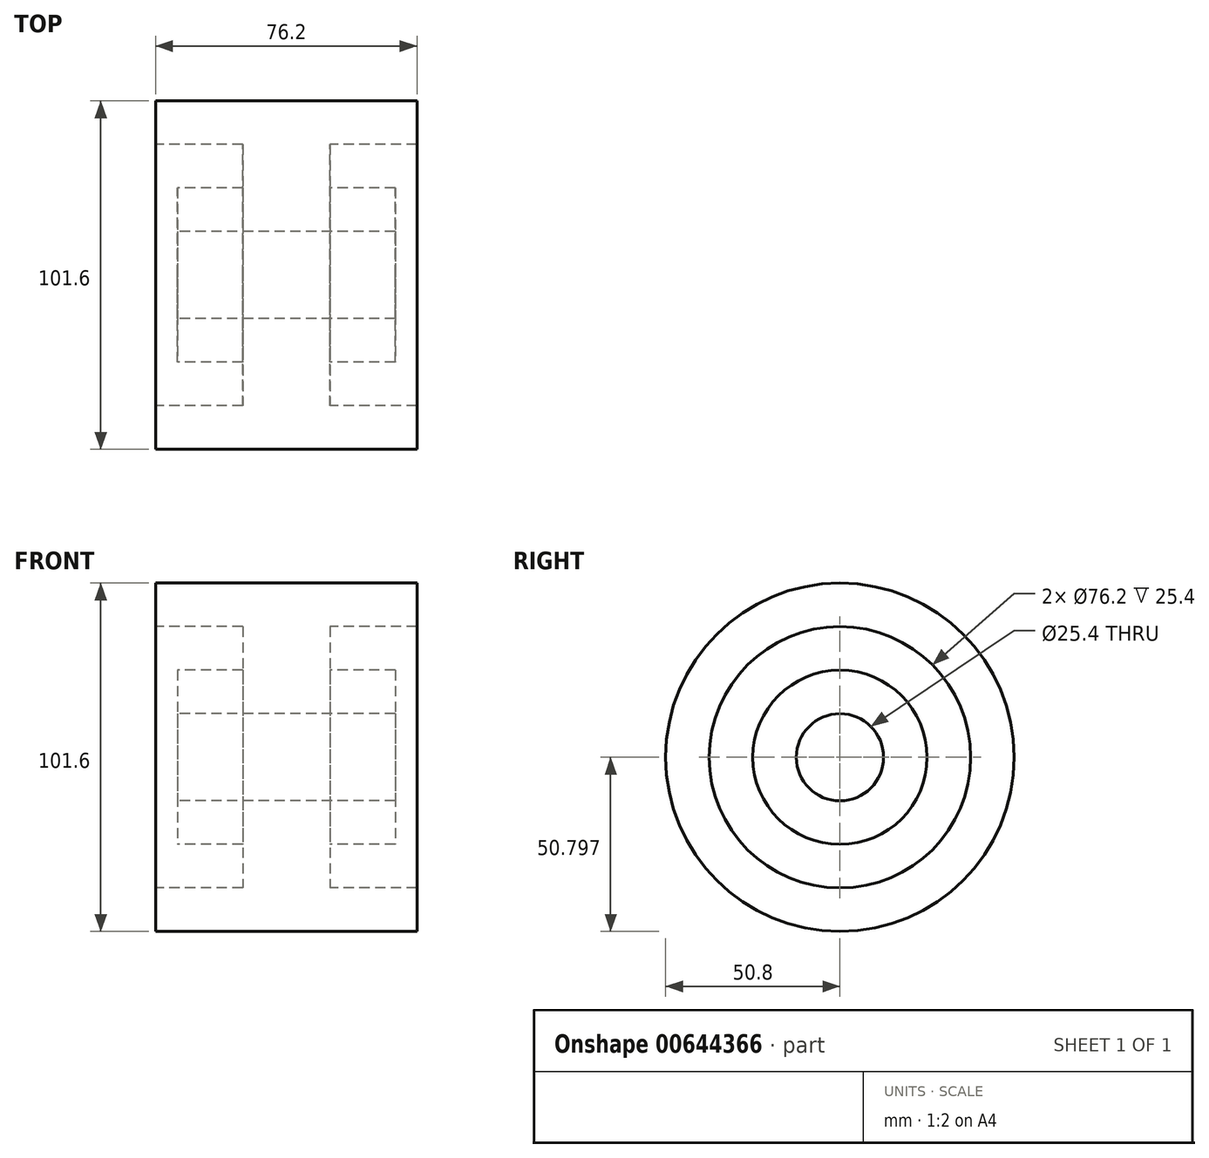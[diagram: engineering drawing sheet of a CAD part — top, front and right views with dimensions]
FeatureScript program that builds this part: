
annotation { "Feature Type Name" : "Feature", "Feature Type Description" : "" }
export const myFeature = defineFeature(function(context is Context, id is Id, definition is map)
    precondition{}
    {
        {
            var Q0;
            Q0=qCreatedBy(makeId("Front.planeOp"),FACE);
            var sketch = newSketch(context, id + "F0", { "sketchPlane" : qUnion([Q0])});
            skLineSegment(sketch, "E0", {"start": v(-87.87, 0) * mm, "end": v(96.65, 0) * mm, "construction": true});
            skLineSegment(sketch, "E1", {"start": v(0, 0) * mm, "end": v(0, 85.08) * mm, "construction": true});
            skLineSegment(sketch, "E2", {"start": v(-27.3, 15.39) * mm, "end": v(36.2, 15.39) * mm});
            skLineSegment(sketch, "E3", {"start": v(36.2, 15.39) * mm, "end": v(36.2, 28.09) * mm});
            skLineSegment(sketch, "E4", {"start": v(36.2, 28.09) * mm, "end": v(17.14, 28.09) * mm});
            skLineSegment(sketch, "E5", {"start": v(17.14, 28.09) * mm, "end": v(17.14, 40.79) * mm});
            skLineSegment(sketch, "E6", {"start": v(17.14, 40.79) * mm, "end": v(42.54, 40.79) * mm});
            skLineSegment(sketch, "E7", {"start": v(42.54, 40.79) * mm, "end": v(42.54, 53.49) * mm});
            skLineSegment(sketch, "E8", {"start": v(42.54, 53.49) * mm, "end": v(-33.66, 53.49) * mm});
            skLineSegment(sketch, "E9", {"start": v(-33.66, 53.49) * mm, "end": v(-33.66, 40.79) * mm});
            skLineSegment(sketch, "E10", {"start": v(-33.66, 40.79) * mm, "end": v(-8.26, 40.79) * mm});
            skLineSegment(sketch, "E11", {"start": v(-8.26, 40.79) * mm, "end": v(-8.26, 28.09) * mm});
            skLineSegment(sketch, "E12", {"start": v(-8.26, 28.09) * mm, "end": v(-27.3, 28.09) * mm});
            skLineSegment(sketch, "E13", {"start": v(-27.3, 28.09) * mm, "end": v(-27.3, 15.39) * mm});
            skSolve(sketch);
        }
        {
            var Q0;
            Q0=qCreatedBy(makeId("Front.planeOp"),FACE);
            var sketch = newSketch(context, id + "F1", { "sketchPlane" : qUnion([Q0])});
            skLineSegment(sketch, "E14.0", {"start": v(-27.3, 2.69) * mm, "end": v(36.2, 2.69) * mm});
            skSolve(sketch);
        }
        {
            var Q0;
            Q0=makeQuery(id+"F0.imprint","IMPRINT",FACE,{"disambiguationData":[TD([[makeQuery(id+"F0.imprint","IMPRINT",EDGE,{"derivedFrom":sQuery(id+"F0.wireOp",EDGE,"E2")}),1.0]])]});
            var Q1;
            Q1=sQuery(id+"F1.wireOp",EDGE,"E14.0");
            revolve(context, id + "F2", {"entities" : qUnion([Q0]), "axis" : qUnion([Q1]), "revolveType" : RevolveType.FULL});
        }
    });
